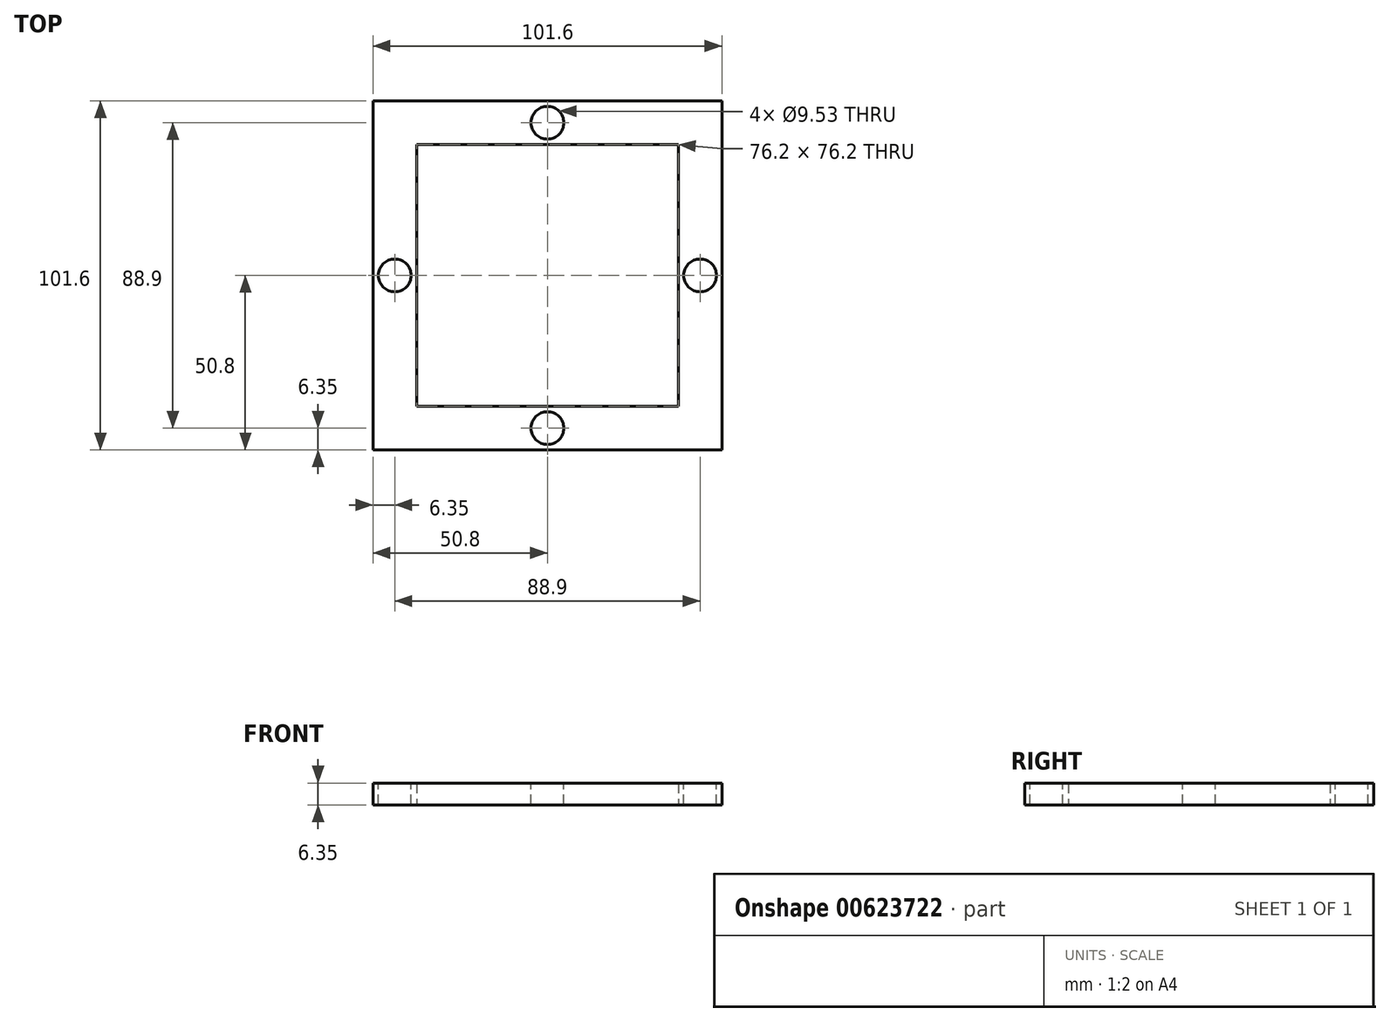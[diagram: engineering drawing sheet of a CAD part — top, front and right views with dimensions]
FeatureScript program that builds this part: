
annotation { "Feature Type Name" : "Feature", "Feature Type Description" : "" }
export const myFeature = defineFeature(function(context is Context, id is Id, definition is map)
    precondition{}
    {
        {
            var Q0;
            Q0=qCreatedBy(makeId("Top.planeOp"),FACE);
            var sketch = newSketch(context, id + "F0", { "sketchPlane" : qUnion([Q0])});
            skLineSegment(sketch, "E0.bottom", {"start": v(50.8, 50.8) * mm, "end": v(-50.8, 50.8) * mm});
            skLineSegment(sketch, "E0.top", {"start": v(50.8, -50.8) * mm, "end": v(-50.8, -50.8) * mm});
            skLineSegment(sketch, "E0.left", {"start": v(50.8, 50.8) * mm, "end": v(50.8, -50.8) * mm});
            skLineSegment(sketch, "E0.right", {"start": v(-50.8, 50.8) * mm, "end": v(-50.8, -50.8) * mm});
            skPoint(sketch, "E0.middle", {"position": v(0, 0) * mm});
            skLineSegment(sketch, "E1.bottom", {"start": v(38.1, 38.1) * mm, "end": v(-38.1, 38.1) * mm});
            skLineSegment(sketch, "E1.top", {"start": v(38.1, -38.1) * mm, "end": v(-38.1, -38.1) * mm});
            skLineSegment(sketch, "E1.left", {"start": v(38.1, 38.1) * mm, "end": v(38.1, -38.1) * mm});
            skLineSegment(sketch, "E1.right", {"start": v(-38.1, 38.1) * mm, "end": v(-38.1, -38.1) * mm});
            skSolve(sketch);
        }
        {
            var Q0;
            Q0=makeQuery(id+"F0.imprint","IMPRINT",FACE,{"disambiguationData":[TD([[makeQuery(id+"F0.imprint","IMPRINT",EDGE,{"derivedFrom":sQuery(id+"F0.wireOp",EDGE,"E0.bottom")}),1.0]])]});
            extrude(context, id + "F1", {"entities" : qUnion([Q0]), "depth" : 6.35 * mm, "offsetDistance" : 25.4 * mm});
        }
        {
            var Q0;
            Q0=makeQuery(id+"F1.opExtrude","CAP_FACE",FACE,{"disambiguationData":[OSD([sQuery(id+"F0.wireOp",EDGE,"E0.bottom"),sQuery(id+"F0.wireOp",EDGE,"E0.top"),sQuery(id+"F0.wireOp",EDGE,"E0.left"),sQuery(id+"F0.wireOp",EDGE,"E0.right"),sQuery(id+"F0.wireOp",EDGE,"E1.bottom"),sQuery(id+"F0.wireOp",EDGE,"E1.top"),sQuery(id+"F0.wireOp",EDGE,"E1.left"),sQuery(id+"F0.wireOp",EDGE,"E1.right")])],"isStart":false});
            var sketch = newSketch(context, id + "F2", { "sketchPlane" : qUnion([Q0])});
            skLineSegment(sketch, "E2", {"start": v(0, 0) * mm, "end": v(0, 44.45) * mm});
            skPoint(sketch, "E2.endSnap0", {"position": v(0, 38.1) * mm});
            skLineSegment(sketch, "E3", {"start": v(0, 0) * mm, "end": v(-44.45, 0) * mm});
            skPoint(sketch, "E3.endSnap0", {"position": v(-38.1, 0) * mm});
            skLineSegment(sketch, "E4.MirrorCS", {"start": v(0, 0) * mm, "end": v(44.45, 0) * mm});
            skLineSegment(sketch, "E5.MirrorCS", {"start": v(0, 0) * mm, "end": v(0, -44.45) * mm});
            skCircle(sketch, "E6", {"center": v(0, 44.45) * mm, "radius": 4.76 * mm});
            skCircle(sketch, "E7", {"center": v(0, -44.45) * mm, "radius": 4.76 * mm});
            skCircle(sketch, "E8", {"center": v(-44.45, 0) * mm, "radius": 4.76 * mm});
            skCircle(sketch, "E9", {"center": v(44.45, 0) * mm, "radius": 4.76 * mm});
            skSolve(sketch);
        }
        {
            var Q0;
            Q0=sQuery(id+"F2.wireOp",VERTEX,"E2.end");
            var Q1;
            Q1=sQuery(id+"F2.wireOp",VERTEX,"E3.end");
            var Q2;
            Q2=sQuery(id+"F2.wireOp",VERTEX,"E4.MirrorCS.end");
            var Q3;
            Q3=sQuery(id+"F2.wireOp",VERTEX,"E7.center");
            var Q4;
            Q4=makeQuery(id+"F1.opExtrude","SWEPT_BODY",BODY,{"disambiguationData":[OSD([sQuery(id+"F0.wireOp",EDGE,"E0.bottom"),sQuery(id+"F0.wireOp",EDGE,"E0.top"),sQuery(id+"F0.wireOp",EDGE,"E0.left"),sQuery(id+"F0.wireOp",EDGE,"E0.right"),sQuery(id+"F0.wireOp",EDGE,"E1.bottom"),sQuery(id+"F0.wireOp",EDGE,"E1.top"),sQuery(id+"F0.wireOp",EDGE,"E1.left"),sQuery(id+"F0.wireOp",EDGE,"E1.right")])]});
            hole(context, id + "F3", {"style" : HoleStyle.SIMPLE, "endStyle" : HoleEndStyle.BLIND, "holeDiameter" : 9.52 * mm, "majorDiameter" : 6.35 * mm, "holeDepth" : 12.7 * mm, "isTappedThrough" : true, "tappedDepth" : 12.7 * mm, "tapClearance" : 3, "locations" : qUnion([Q0, Q1, Q2, Q3]), "scope" : qUnion([Q4])});
        }
    });
